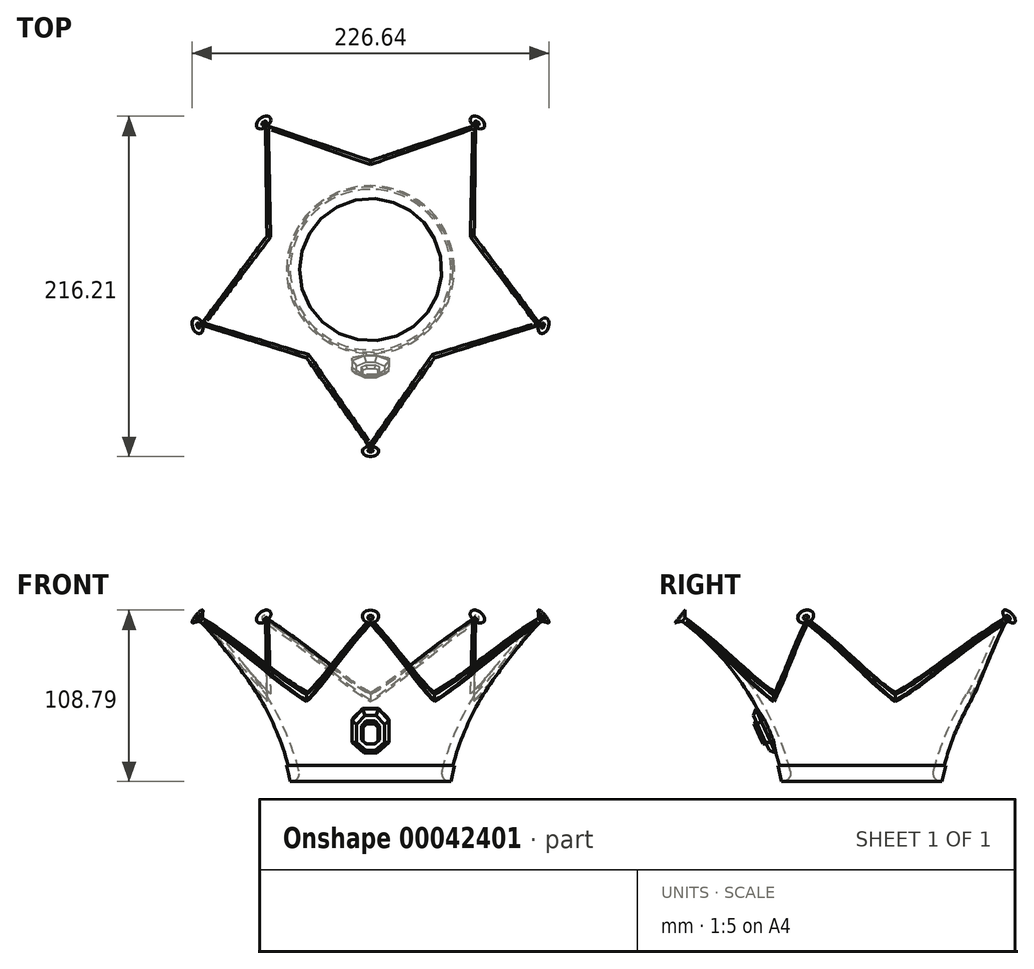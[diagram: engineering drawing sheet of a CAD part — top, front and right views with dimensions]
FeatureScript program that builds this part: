
annotation { "Feature Type Name" : "Feature", "Feature Type Description" : "" }
export const myFeature = defineFeature(function(context is Context, id is Id, definition is map)
    precondition{}
    {
        {
            var Q0;
            Q0=qCreatedBy(makeId("Front.planeOp"),FACE);
            var sketch = newSketch(context, id + "F0", { "sketchPlane" : qUnion([Q0])});
            skLineSegment(sketch, "E0", {"start": v(0, 0) * mm, "end": v(0, 100) * mm, "construction": true});
            skLineSegment(sketch, "E1", {"start": v(0, 0) * mm, "end": v(-50, 0) * mm, "construction": true});
            skArc(sketch, "E2", {"start": v(-50, 0) * mm, "mid": v(-71.94, 55.6) * mm, "end": v(-111.98, 100) * mm});
            skLineSegment(sketch, "E3", {"start": v(-111.98, 100) * mm, "end": v(-214.57, -32.8) * mm, "construction": true});
            skLineSegment(sketch, "E4", {"start": v(-111.98, 100) * mm, "end": v(-110.15, 102.37) * mm});
            skArc(sketch, "E5", {"start": v(-43.88, 0) * mm, "mid": v(-67.74, 57.2) * mm, "end": v(-110.15, 102.37) * mm});
            skLineSegment(sketch, "E6", {"start": v(-50, 0) * mm, "end": v(-43.88, 0) * mm});
            skLineSegment(sketch, "E7", {"start": v(-50, 0) * mm, "end": v(-51, 0) * mm});
            skLineSegment(sketch, "E8", {"start": v(-52.31, 10) * mm, "end": v(-53.31, 10) * mm});
            skLineSegment(sketch, "E9", {"start": v(-53.31, 10) * mm, "end": v(-51, 0) * mm});
            skLineSegment(sketch, "E10", {"start": v(-53.31, 10) * mm, "end": v(-53.31, 0) * mm, "construction": true});
            skSolve(sketch);
        }
        {
            var Q0;
            Q0 = qSketchRegion(id + "F0", true);
            var Q1;
            Q1=sQuery(id+"F0.wireOp",EDGE,"E0");
            revolve(context, id + "F1", {"entities" : qUnion([Q0]), "axis" : qUnion([Q1]), "revolveType" : RevolveType.FULL});
        }
        {
            var Q0;
            Q0=qCreatedBy(makeId("Top.planeOp"),FACE);
            var sketch = newSketch(context, id + "F2", { "sketchPlane" : qUnion([Q0])});
            skLineSegment(sketch, "E11", {"start": v(0, 0) * mm, "end": v(0, -111.98) * mm, "construction": true});
            skCircle(sketch, "E12.0", {"center": v(0, 0) * mm, "radius": 111.98 * mm, "construction": true});
            skLineSegment(sketch, "E13", {"start": v(-1, -111.98) * mm, "end": v(1, -111.98) * mm});
            skLineSegment(sketch, "E14", {"start": v(-1, -111.98) * mm, "end": v(-40.68, -56) * mm});
            skPoint(sketch, "E15", {"position": v(0, -56) * mm});
            skLineSegment(sketch, "E16.MirrorCS", {"start": v(1, -111.98) * mm, "end": v(40.68, -56) * mm});
            skLineSegment(sketch, "E17.1.0", {"start": v(106.2, -35.56) * mm, "end": v(106.8, -33.65) * mm});
            skLineSegment(sketch, "E17.1.1", {"start": v(106.2, -35.56) * mm, "end": v(40.68, -56) * mm});
            skLineSegment(sketch, "E17.1.2", {"start": v(106.8, -33.65) * mm, "end": v(65.82, 21.39) * mm});
            skLineSegment(sketch, "E17.2.0", {"start": v(66.63, 90) * mm, "end": v(65.01, 91.18) * mm});
            skLineSegment(sketch, "E17.2.1", {"start": v(66.63, 90) * mm, "end": v(65.82, 21.39) * mm});
            skLineSegment(sketch, "E17.2.2", {"start": v(65.01, 91.18) * mm, "end": v(0, 69.2) * mm});
            skLineSegment(sketch, "E17.3.0", {"start": v(-65.01, 91.18) * mm, "end": v(-66.63, 90) * mm});
            skLineSegment(sketch, "E17.3.1", {"start": v(-65.01, 91.18) * mm, "end": v(0, 69.2) * mm});
            skLineSegment(sketch, "E17.3.2", {"start": v(-66.63, 90) * mm, "end": v(-65.82, 21.39) * mm});
            skLineSegment(sketch, "E17.4.0", {"start": v(-106.8, -33.65) * mm, "end": v(-106.2, -35.56) * mm});
            skLineSegment(sketch, "E17.4.1", {"start": v(-106.8, -33.65) * mm, "end": v(-65.82, 21.39) * mm});
            skLineSegment(sketch, "E17.4.2", {"start": v(-106.2, -35.56) * mm, "end": v(-40.68, -56) * mm});
            skCircle(sketch, "E18", {"center": v(0, 0) * mm, "radius": 111.99 * mm});
            skCircle(sketch, "E19.0", {"center": v(0, 0) * mm, "radius": 51 * mm, "construction": true});
            skPoint(sketch, "E20", {"position": v(0, -51) * mm});
            skLineSegment(sketch, "E21", {"start": v(0, -56) * mm, "end": v(0, -67) * mm, "construction": true});
            skSolve(sketch);
        }
        {
            var Q0;
            {var subQ2=sQuery(id+"F2.wireOp",EDGE,"E14");Q0=makeQuery(id+"F2.imprint","IMPRINT",FACE,{"disambiguationData":[TD([[makeQuery(id+"F2.imprint","IMPRINT",EDGE,{"derivedFrom":subQ2}),1.0]])]});}
            var Q1;
            {var subQ2=sQuery(id+"F2.wireOp",EDGE,"E16.MirrorCS");Q1=makeQuery(id+"F2.imprint","IMPRINT",FACE,{"disambiguationData":[TD([[makeQuery(id+"F2.imprint","IMPRINT",EDGE,{"derivedFrom":subQ2}),-1.0]])]});}
            var Q2;
            {var subQ2=sQuery(id+"F2.wireOp",EDGE,"E17.1.2");Q2=makeQuery(id+"F2.imprint","IMPRINT",FACE,{"disambiguationData":[TD([[makeQuery(id+"F2.imprint","IMPRINT",EDGE,{"derivedFrom":subQ2}),-1.0]])]});}
            var Q3;
            {var subQ2=sQuery(id+"F2.wireOp",EDGE,"E17.3.2");Q3=makeQuery(id+"F2.imprint","IMPRINT",FACE,{"disambiguationData":[TD([[makeQuery(id+"F2.imprint","IMPRINT",EDGE,{"derivedFrom":subQ2}),-1.0]])]});}
            var Q4;
            {var subQ2=sQuery(id+"F2.wireOp",EDGE,"E17.2.2");Q4=makeQuery(id+"F2.imprint","IMPRINT",FACE,{"disambiguationData":[TD([[makeQuery(id+"F2.imprint","IMPRINT",EDGE,{"derivedFrom":subQ2}),-1.0]])]});}
            extrude(context, id + "F3", {"entities" : qUnion([Q0, Q1, Q2, Q3, Q4]), "operationType" : NewBodyOperationType.REMOVE, "endBound" : BoundingType.THROUGH_ALL, "depth" : 25 * mm});
        }
        {
            var Q0;
            Q0=qCreatedBy(makeId("Right.planeOp"),FACE);
            var sketch = newSketch(context, id + "F4", { "sketchPlane" : qUnion([Q0])});
            skPoint(sketch, "E22.0", {"position": v(-110.12, 102.37) * mm});
            skPoint(sketch, "E23.0", {"position": v(-111.98, 100) * mm});
            skLineSegment(sketch, "E24", {"start": v(-110.12, 102.37) * mm, "end": v(-111.98, 100) * mm, "construction": true});
            skLineSegment(sketch, "E25", {"start": v(-111.05, 101.19) * mm, "end": v(-122.87, 110.42) * mm});
            skLineSegment(sketch, "E26", {"start": v(-111.05, 101.19) * mm, "end": v(-110.12, 102.37) * mm});
            skLineSegment(sketch, "E27", {"start": v(-110.12, 102.37) * mm, "end": v(-112.2, 104) * mm});
            skArc(sketch, "E28", {"start": v(-112.3, 108.8) * mm, "mid": v(-112.44, 106.39) * mm, "end": v(-112.2, 104) * mm});
            skLineSegment(sketch, "E29", {"start": v(-112.3, 108.8) * mm, "end": v(-112.3, 108.8) * mm});
            skArc(sketch, "E30", {"start": v(-113.84, 105.52) * mm, "mid": v(-112.9, 107.07) * mm, "end": v(-112.3, 108.8) * mm});
            skArc(sketch, "E31", {"start": v(-113.84, 105.52) * mm, "mid": v(-116.12, 112.09) * mm, "end": v(-122.87, 110.42) * mm});
            skSolve(sketch);
        }
        {
            var Q0;
            Q0 = qSketchRegion(id + "F4", true);
            var Q1;
            Q1=sQuery(id+"F4.wireOp",EDGE,"E25");
            revolve(context, id + "F5", {"entities" : qUnion([Q0]), "axis" : qUnion([Q1]), "revolveType" : RevolveType.FULL});
        }
        {
            var Q0;
            Q0=makeQuery(id+"F5.opRevolve","SWEPT_BODY",BODY,{"disambiguationData":[OSD([sQuery(id+"F4.wireOp",EDGE,"E25"),sQuery(id+"F4.wireOp",EDGE,"E26"),sQuery(id+"F4.wireOp",EDGE,"E27"),sQuery(id+"F4.wireOp",EDGE,"E28"),sQuery(id+"F4.wireOp",EDGE,"E30"),sQuery(id+"F4.wireOp",EDGE,"E31")])]});
            var Q1;
            Q1=sQuery(id+"F0.wireOp",EDGE,"E0");
            circularPattern(context, id + "F6", {"operationType" : NewBodyOperationType.ADD, "entities" : qUnion([Q0]), "axis" : qUnion([Q1]), "angle" : 72 * degree, "instanceCount" : 5});
        }
        {
            var Q0;
            Q0=makeQuery(id+"F3.boolean.opBoolean","INTERSECT",VERTEX,{"derivedFrom":[makeQuery(id+"F1.opRevolve","SWEPT_FACE",FACE,{"disambiguationData":[OSD([sQuery(id+"F0.wireOp",EDGE,"E2")])]}),makeQuery(id+"F1.opRevolve","SWEPT_FACE",FACE,{"disambiguationData":[OSD([sQuery(id+"F0.wireOp",EDGE,"E4")])]}),makeQuery(id+"F3.opExtrude","SWEPT_FACE",FACE,{"disambiguationData":[OSD([sQuery(id+"F2.wireOp",EDGE,"E14")])]})]});
            var Q1;
            Q1=makeQuery(id+"F3.boolean.opBoolean","INTERSECT",VERTEX,{"derivedFrom":[makeQuery(id+"F1.opRevolve","SWEPT_FACE",FACE,{"disambiguationData":[OSD([sQuery(id+"F0.wireOp",EDGE,"E2")])]}),makeQuery(id+"F1.opRevolve","SWEPT_FACE",FACE,{"disambiguationData":[OSD([sQuery(id+"F0.wireOp",EDGE,"E4")])]}),makeQuery(id+"F3.opExtrude","SWEPT_FACE",FACE,{"disambiguationData":[OSD([sQuery(id+"F2.wireOp",EDGE,"E16.MirrorCS")])]})]});
            var Q2;
            Q2=sQuery(id+"F2.wireOp",VERTEX,"E21.end");
            cPlane(context, id + "F7", {"entities" : qUnion([Q0, Q1, Q2]), "cplaneType" : CPlaneType.THREE_POINT, "offset" : 150 * mm, "width" : 150 * mm, "height" : 150 * mm});
        }
        {
            var Q0;
            Q0=qCreatedBy(id+"F7.planeOp",FACE);
            cPlane(context, id + "F8", {"entities" : qUnion([Q0]), "cplaneType" : CPlaneType.OFFSET, "offset" : 20 * mm, "oppositeDirection" : true, "width" : 150 * mm, "height" : 150 * mm});
        }
        {
            var Q0;
            Q0=qCreatedBy(id+"F8.planeOp",FACE);
            var sketch = newSketch(context, id + "F9", { "sketchPlane" : qUnion([Q0])});
            skLineSegment(sketch, "E32.0", {"start": v(0, 0) * mm, "end": v(0, 91.2) * mm, "construction": true});
            skLineSegment(sketch, "E33.0", {"start": v(-1, 45.94) * mm, "end": v(1, 45.94) * mm, "construction": true});
            skPoint(sketch, "E34.0", {"position": v(-40.68, 69.52) * mm});
            skPoint(sketch, "E35.0", {"position": v(40.68, 69.52) * mm});
            skLineSegment(sketch, "E36", {"start": v(-40.68, 69.52) * mm, "end": v(40.68, 69.52) * mm, "construction": true});
            skLineSegment(sketch, "E37", {"start": v(-5, 69.52) * mm, "end": v(5, 69.52) * mm});
            skPoint(sketch, "E38", {"position": v(0, 69.52) * mm});
            skLineSegment(sketch, "E39", {"start": v(-5, 69.52) * mm, "end": v(-11.83, 61.33) * mm});
            skLineSegment(sketch, "E40", {"start": v(-11.83, 61.33) * mm, "end": v(-11.83, 46.33) * mm});
            skLineSegment(sketch, "E41", {"start": v(-11.83, 46.33) * mm, "end": v(-4.17, 38.9) * mm});
            skLineSegment(sketch, "E42", {"start": v(-4.17, 38.9) * mm, "end": v(0, 38.9) * mm});
            skLineSegment(sketch, "E43.MirrorCS", {"start": v(5, 69.52) * mm, "end": v(11.83, 61.33) * mm});
            skLineSegment(sketch, "E44.MirrorCS", {"start": v(11.83, 61.33) * mm, "end": v(11.83, 46.33) * mm});
            skLineSegment(sketch, "E45.MirrorCS", {"start": v(11.83, 46.33) * mm, "end": v(4.17, 38.9) * mm});
            skLineSegment(sketch, "E46.MirrorCS", {"start": v(4.17, 38.9) * mm, "end": v(0, 38.9) * mm});
            skSolve(sketch);
        }
        {
            var Q0;
            Q0 = qSketchRegion(id + "F9", true);
            extrude(context, id + "F10", {"entities" : qUnion([Q0]), "operationType" : NewBodyOperationType.ADD, "depth" : 4.5 * mm, "hasSecondDirection" : true, "secondDirectionOppositeDirection" : true, "secondDirectionDepth" : 1 * mm});
        }
        {
            var Q0;
            Q0=makeQuery(id+"F10.opExtrude","CAP_EDGE",EDGE,{"disambiguationData":[OSD([sQuery(id+"F9.wireOp",EDGE,"E37")])],"isStart":false});
            var Q1;
            Q1=makeQuery(id+"F10.opExtrude","CAP_EDGE",EDGE,{"disambiguationData":[OSD([sQuery(id+"F9.wireOp",EDGE,"E39")])],"isStart":false});
            var Q2;
            Q2=makeQuery(id+"F10.opExtrude","CAP_EDGE",EDGE,{"disambiguationData":[OSD([sQuery(id+"F9.wireOp",EDGE,"E43.MirrorCS")])],"isStart":false});
            var Q3;
            Q3=makeQuery(id+"F10.opExtrude","CAP_EDGE",EDGE,{"disambiguationData":[OSD([sQuery(id+"F9.wireOp",EDGE,"E44.MirrorCS")])],"isStart":false});
            var Q4;
            Q4=makeQuery(id+"F10.opExtrude","CAP_EDGE",EDGE,{"disambiguationData":[OSD([sQuery(id+"F9.wireOp",EDGE,"E45.MirrorCS")])],"isStart":false});
            var Q5;
            Q5=makeQuery(id+"F10.opExtrude","CAP_EDGE",EDGE,{"disambiguationData":[OSD([sQuery(id+"F9.wireOp",EDGE,"E41")])],"isStart":false});
            var Q6;
            Q6=makeQuery(id+"F10.opExtrude","CAP_EDGE",EDGE,{"disambiguationData":[OSD([sQuery(id+"F9.wireOp",EDGE,"E42"),sQuery(id+"F9.wireOp",EDGE,"E46.MirrorCS")])],"isStart":false});
            var Q7;
            Q7=makeQuery(id+"F10.opExtrude","CAP_EDGE",EDGE,{"disambiguationData":[OSD([sQuery(id+"F9.wireOp",EDGE,"E40")])],"isStart":false});
            chamfer(context, id + "F11", {"entities" : qUnion([Q0, Q1, Q2, Q3, Q4, Q5, Q6, Q7]), "width" : 3 * mm, "tangentPropagation" : true});
        }
        {
            var Q0;
            Q0=makeQuery(id+"F10.opExtrude","CAP_FACE",FACE,{"disambiguationData":[OSD([sQuery(id+"F9.wireOp",EDGE,"E37"),sQuery(id+"F9.wireOp",EDGE,"E39"),sQuery(id+"F9.wireOp",EDGE,"E40"),sQuery(id+"F9.wireOp",EDGE,"E41"),sQuery(id+"F9.wireOp",EDGE,"E42"),sQuery(id+"F9.wireOp",EDGE,"E43.MirrorCS"),sQuery(id+"F9.wireOp",EDGE,"E44.MirrorCS"),sQuery(id+"F9.wireOp",EDGE,"E45.MirrorCS"),sQuery(id+"F9.wireOp",EDGE,"E46.MirrorCS")])],"isStart":false});
            var sketch = newSketch(context, id + "F12", { "sketchPlane" : qUnion([Q0])});
            skLineSegment(sketch, "E47", {"start": v(-3, 62.47) * mm, "end": v(0, 62.47) * mm});
            skLineSegment(sketch, "E48", {"start": v(-3, 62.47) * mm, "end": v(-5.72, 59.21) * mm});
            skLineSegment(sketch, "E49", {"start": v(-5.72, 49.21) * mm, "end": v(-3, 46.58) * mm});
            skLineSegment(sketch, "E50", {"start": v(-3, 46.58) * mm, "end": v(0, 46.58) * mm});
            skLineSegment(sketch, "E51", {"start": v(0, 66.52) * mm, "end": v(0, 41.9) * mm, "construction": true});
            skLineSegment(sketch, "E52", {"start": v(-5.72, 54.21) * mm, "end": v(0, 54.21) * mm, "construction": true});
            skLineSegment(sketch, "E53", {"start": v(-5.72, 59.21) * mm, "end": v(-5.72, 49.21) * mm});
            skLineSegment(sketch, "E54.MirrorCS", {"start": v(3, 62.47) * mm, "end": v(0, 62.47) * mm});
            skLineSegment(sketch, "E55.MirrorCS", {"start": v(3, 62.47) * mm, "end": v(5.72, 59.21) * mm});
            skLineSegment(sketch, "E56.MirrorCS", {"start": v(5.72, 59.21) * mm, "end": v(5.72, 49.21) * mm});
            skLineSegment(sketch, "E57.MirrorCS", {"start": v(5.72, 49.21) * mm, "end": v(3, 46.58) * mm});
            skLineSegment(sketch, "E58.MirrorCS", {"start": v(3, 46.58) * mm, "end": v(0, 46.58) * mm});
            skSolve(sketch);
        }
        {
            var Q0;
            Q0=makeQuery(id+"F12.imprint","IMPRINT",FACE,{"disambiguationData":[TD([[makeQuery(id+"F12.imprint","IMPRINT",EDGE,{"derivedFrom":sQuery(id+"F12.wireOp",EDGE,"E47")}),1.0]])]});
            cPlane(context, id + "F13", {"entities" : qUnion([Q0]), "cplaneType" : CPlaneType.OFFSET, "offset" : 2 * mm, "width" : 150 * mm, "height" : 150 * mm});
        }
        {
            var Q0;
            Q0=qCreatedBy(id+"F13.planeOp",FACE);
            var sketch = newSketch(context, id + "F14", { "sketchPlane" : qUnion([Q0])});
            skLineSegment(sketch, "E59.0", {"start": v(-3, 62.47) * mm, "end": v(-5.72, 59.21) * mm, "construction": true});
            skLineSegment(sketch, "E60.0", {"start": v(-3, 62.47) * mm, "end": v(0, 62.47) * mm, "construction": true});
            skLineSegment(sketch, "E61.0", {"start": v(3, 62.47) * mm, "end": v(0, 62.47) * mm, "construction": true});
            skLineSegment(sketch, "E62.0", {"start": v(3, 62.47) * mm, "end": v(5.72, 59.21) * mm, "construction": true});
            skLineSegment(sketch, "E63.0", {"start": v(5.72, 59.21) * mm, "end": v(5.72, 49.21) * mm, "construction": true});
            skLineSegment(sketch, "E64.0", {"start": v(5.72, 49.21) * mm, "end": v(3, 46.58) * mm, "construction": true});
            skLineSegment(sketch, "E65.0", {"start": v(3, 46.58) * mm, "end": v(0, 46.58) * mm, "construction": true});
            skLineSegment(sketch, "E66.0", {"start": v(-3, 46.58) * mm, "end": v(0, 46.58) * mm, "construction": true});
            skLineSegment(sketch, "E67.0", {"start": v(-5.72, 49.21) * mm, "end": v(-3, 46.58) * mm, "construction": true});
            skLineSegment(sketch, "E68.0", {"start": v(-5.72, 59.21) * mm, "end": v(-5.72, 49.21) * mm, "construction": true});
            skLineSegment(sketch, "E69.0", {"start": v(-2.53, 61.47) * mm, "end": v(0, 61.47) * mm});
            skLineSegment(sketch, "E69.1", {"start": v(2.53, 61.47) * mm, "end": v(0, 61.47) * mm});
            skLineSegment(sketch, "E69.2", {"start": v(-2.53, 61.47) * mm, "end": v(-4.72, 58.85) * mm});
            skLineSegment(sketch, "E69.3", {"start": v(2.53, 61.47) * mm, "end": v(4.72, 58.85) * mm});
            skLineSegment(sketch, "E69.4", {"start": v(4.72, 58.85) * mm, "end": v(4.72, 49.63) * mm});
            skLineSegment(sketch, "E69.5", {"start": v(4.72, 49.63) * mm, "end": v(2.6, 47.58) * mm});
            skLineSegment(sketch, "E69.6", {"start": v(-4.72, 58.85) * mm, "end": v(-4.72, 49.63) * mm});
            skLineSegment(sketch, "E69.7", {"start": v(-4.72, 49.63) * mm, "end": v(-2.6, 47.58) * mm});
            skLineSegment(sketch, "E69.8", {"start": v(-2.6, 47.58) * mm, "end": v(0, 47.58) * mm});
            skLineSegment(sketch, "E69.9", {"start": v(2.6, 47.58) * mm, "end": v(0, 47.58) * mm});
            skSolve(sketch);
        }
        {
            var Q1;
            Q1=makeQuery(id+"F12.imprint","IMPRINT",FACE,{"disambiguationData":[TD([[makeQuery(id+"F12.imprint","IMPRINT",EDGE,{"derivedFrom":sQuery(id+"F12.wireOp",EDGE,"E47")}),-1.0]])]});
            var Q2;
            Q2=makeQuery(id+"F14.imprint","IMPRINT",FACE,{"disambiguationData":[TD([[makeQuery(id+"F14.imprint","IMPRINT",EDGE,{"derivedFrom":sQuery(id+"F14.wireOp",EDGE,"E69.0")}),-1.0]])]});
            loft(context, id + "F15", {"operationType" : NewBodyOperationType.ADD, "sheetProfilesArray" : [{ "sheetProfileEntities" : qUnion([Q1]) }, { "sheetProfileEntities" : qUnion([Q2]) }]});
        }
        {
            var Q0;
            Q0=makeQuery(id+"F1.opRevolve","SWEPT_EDGE",EDGE,{"disambiguationData":[OSD([sQuery(id+"F0.wireOp",EDGE,"E5"),sQuery(id+"F0.wireOp",EDGE,"E6")])]});
            fillet(context, id + "F16", {"entities" : qUnion([Q0]), "radius" : 5 * mm, "tangentPropagation" : true, "allowEdgeOverflow" : false});
        }
        {
            var Q0;
            Q0=makeQuery(id+"F3.boolean.opBoolean","INTERSECT",EDGE,{"derivedFrom":[makeQuery(id+"F1.opRevolve","SWEPT_FACE",FACE,{"disambiguationData":[OSD([sQuery(id+"F0.wireOp",EDGE,"E2")])]}),makeQuery(id+"F3.opExtrude","SWEPT_FACE",FACE,{"disambiguationData":[OSD([sQuery(id+"F2.wireOp",EDGE,"E16.MirrorCS")])]})]});
            var Q1;
            Q1=makeQuery(id+"F3.boolean.opBoolean","INTERSECT",EDGE,{"derivedFrom":[makeQuery(id+"F1.opRevolve","SWEPT_FACE",FACE,{"disambiguationData":[OSD([sQuery(id+"F0.wireOp",EDGE,"E2")])]}),makeQuery(id+"F3.opExtrude","SWEPT_FACE",FACE,{"disambiguationData":[OSD([sQuery(id+"F2.wireOp",EDGE,"E14")])]})]});
            var Q2;
            Q2=makeQuery(id+"F3.boolean.opBoolean","INTERSECT",EDGE,{"derivedFrom":[makeQuery(id+"F1.opRevolve","SWEPT_FACE",FACE,{"disambiguationData":[OSD([sQuery(id+"F0.wireOp",EDGE,"E5")])]}),makeQuery(id+"F3.opExtrude","SWEPT_FACE",FACE,{"disambiguationData":[OSD([sQuery(id+"F2.wireOp",EDGE,"E14")])]})]});
            var Q3;
            Q3=makeQuery(id+"F3.boolean.opBoolean","INTERSECT",EDGE,{"derivedFrom":[makeQuery(id+"F1.opRevolve","SWEPT_FACE",FACE,{"disambiguationData":[OSD([sQuery(id+"F0.wireOp",EDGE,"E5")])]}),makeQuery(id+"F3.opExtrude","SWEPT_FACE",FACE,{"disambiguationData":[OSD([sQuery(id+"F2.wireOp",EDGE,"E16.MirrorCS")])]})]});
            var Q4;
            Q4=makeQuery(id+"F3.boolean.opBoolean","INTERSECT",EDGE,{"derivedFrom":[makeQuery(id+"F1.opRevolve","SWEPT_FACE",FACE,{"disambiguationData":[OSD([sQuery(id+"F0.wireOp",EDGE,"E2")])]}),makeQuery(id+"F3.opExtrude","SWEPT_FACE",FACE,{"disambiguationData":[OSD([sQuery(id+"F2.wireOp",EDGE,"E17.4.2")])]})]});
            var Q5;
            Q5=makeQuery(id+"F3.boolean.opBoolean","INTERSECT",EDGE,{"derivedFrom":[makeQuery(id+"F1.opRevolve","SWEPT_FACE",FACE,{"disambiguationData":[OSD([sQuery(id+"F0.wireOp",EDGE,"E5")])]}),makeQuery(id+"F3.opExtrude","SWEPT_FACE",FACE,{"disambiguationData":[OSD([sQuery(id+"F2.wireOp",EDGE,"E17.4.2")])]})]});
            var Q6;
            Q6=makeQuery(id+"F3.boolean.opBoolean","INTERSECT",EDGE,{"derivedFrom":[makeQuery(id+"F1.opRevolve","SWEPT_FACE",FACE,{"disambiguationData":[OSD([sQuery(id+"F0.wireOp",EDGE,"E2")])]}),makeQuery(id+"F3.opExtrude","SWEPT_FACE",FACE,{"disambiguationData":[OSD([sQuery(id+"F2.wireOp",EDGE,"E17.4.1")])]})]});
            var Q7;
            Q7=makeQuery(id+"F3.boolean.opBoolean","INTERSECT",EDGE,{"derivedFrom":[makeQuery(id+"F1.opRevolve","SWEPT_FACE",FACE,{"disambiguationData":[OSD([sQuery(id+"F0.wireOp",EDGE,"E5")])]}),makeQuery(id+"F3.opExtrude","SWEPT_FACE",FACE,{"disambiguationData":[OSD([sQuery(id+"F2.wireOp",EDGE,"E17.4.1")])]})]});
            var Q8;
            Q8=makeQuery(id+"F3.boolean.opBoolean","INTERSECT",EDGE,{"derivedFrom":[makeQuery(id+"F1.opRevolve","SWEPT_FACE",FACE,{"disambiguationData":[OSD([sQuery(id+"F0.wireOp",EDGE,"E2")])]}),makeQuery(id+"F3.opExtrude","SWEPT_FACE",FACE,{"disambiguationData":[OSD([sQuery(id+"F2.wireOp",EDGE,"E17.3.2")])]})]});
            var Q9;
            Q9=makeQuery(id+"F3.boolean.opBoolean","INTERSECT",EDGE,{"derivedFrom":[makeQuery(id+"F1.opRevolve","SWEPT_FACE",FACE,{"disambiguationData":[OSD([sQuery(id+"F0.wireOp",EDGE,"E5")])]}),makeQuery(id+"F3.opExtrude","SWEPT_FACE",FACE,{"disambiguationData":[OSD([sQuery(id+"F2.wireOp",EDGE,"E17.3.2")])]})]});
            var Q10;
            Q10=makeQuery(id+"F3.boolean.opBoolean","INTERSECT",EDGE,{"derivedFrom":[makeQuery(id+"F1.opRevolve","SWEPT_FACE",FACE,{"disambiguationData":[OSD([sQuery(id+"F0.wireOp",EDGE,"E5")])]}),makeQuery(id+"F3.opExtrude","SWEPT_FACE",FACE,{"disambiguationData":[OSD([sQuery(id+"F2.wireOp",EDGE,"E17.1.1")])]})]});
            var Q11;
            Q11=makeQuery(id+"F3.boolean.opBoolean","INTERSECT",EDGE,{"derivedFrom":[makeQuery(id+"F1.opRevolve","SWEPT_FACE",FACE,{"disambiguationData":[OSD([sQuery(id+"F0.wireOp",EDGE,"E2")])]}),makeQuery(id+"F3.opExtrude","SWEPT_FACE",FACE,{"disambiguationData":[OSD([sQuery(id+"F2.wireOp",EDGE,"E17.1.1")])]})]});
            var Q12;
            Q12=makeQuery(id+"F3.boolean.opBoolean","INTERSECT",EDGE,{"derivedFrom":[makeQuery(id+"F1.opRevolve","SWEPT_FACE",FACE,{"disambiguationData":[OSD([sQuery(id+"F0.wireOp",EDGE,"E5")])]}),makeQuery(id+"F3.opExtrude","SWEPT_FACE",FACE,{"disambiguationData":[OSD([sQuery(id+"F2.wireOp",EDGE,"E17.1.2")])]})]});
            var Q13;
            Q13=makeQuery(id+"F3.boolean.opBoolean","INTERSECT",EDGE,{"derivedFrom":[makeQuery(id+"F1.opRevolve","SWEPT_FACE",FACE,{"disambiguationData":[OSD([sQuery(id+"F0.wireOp",EDGE,"E2")])]}),makeQuery(id+"F3.opExtrude","SWEPT_FACE",FACE,{"disambiguationData":[OSD([sQuery(id+"F2.wireOp",EDGE,"E17.1.2")])]})]});
            var Q14;
            Q14=makeQuery(id+"F3.boolean.opBoolean","INTERSECT",EDGE,{"derivedFrom":[makeQuery(id+"F1.opRevolve","SWEPT_FACE",FACE,{"disambiguationData":[OSD([sQuery(id+"F0.wireOp",EDGE,"E2")])]}),makeQuery(id+"F3.opExtrude","SWEPT_FACE",FACE,{"disambiguationData":[OSD([sQuery(id+"F2.wireOp",EDGE,"E17.2.1")])]})]});
            var Q15;
            Q15=makeQuery(id+"F3.boolean.opBoolean","INTERSECT",EDGE,{"derivedFrom":[makeQuery(id+"F1.opRevolve","SWEPT_FACE",FACE,{"disambiguationData":[OSD([sQuery(id+"F0.wireOp",EDGE,"E5")])]}),makeQuery(id+"F3.opExtrude","SWEPT_FACE",FACE,{"disambiguationData":[OSD([sQuery(id+"F2.wireOp",EDGE,"E17.2.1")])]})]});
            var Q16;
            Q16=makeQuery(id+"F3.boolean.opBoolean","INTERSECT",EDGE,{"derivedFrom":[makeQuery(id+"F1.opRevolve","SWEPT_FACE",FACE,{"disambiguationData":[OSD([sQuery(id+"F0.wireOp",EDGE,"E2")])]}),makeQuery(id+"F3.opExtrude","SWEPT_FACE",FACE,{"disambiguationData":[OSD([sQuery(id+"F2.wireOp",EDGE,"E17.2.2")])]})]});
            var Q17;
            Q17=makeQuery(id+"F3.boolean.opBoolean","INTERSECT",EDGE,{"derivedFrom":[makeQuery(id+"F1.opRevolve","SWEPT_FACE",FACE,{"disambiguationData":[OSD([sQuery(id+"F0.wireOp",EDGE,"E5")])]}),makeQuery(id+"F3.opExtrude","SWEPT_FACE",FACE,{"disambiguationData":[OSD([sQuery(id+"F2.wireOp",EDGE,"E17.2.2")])]})]});
            var Q18;
            Q18=makeQuery(id+"F3.boolean.opBoolean","INTERSECT",EDGE,{"derivedFrom":[makeQuery(id+"F1.opRevolve","SWEPT_FACE",FACE,{"disambiguationData":[OSD([sQuery(id+"F0.wireOp",EDGE,"E2")])]}),makeQuery(id+"F3.opExtrude","SWEPT_FACE",FACE,{"disambiguationData":[OSD([sQuery(id+"F2.wireOp",EDGE,"E17.3.1")])]})]});
            var Q19;
            Q19=makeQuery(id+"F3.boolean.opBoolean","INTERSECT",EDGE,{"derivedFrom":[makeQuery(id+"F1.opRevolve","SWEPT_FACE",FACE,{"disambiguationData":[OSD([sQuery(id+"F0.wireOp",EDGE,"E5")])]}),makeQuery(id+"F3.opExtrude","SWEPT_FACE",FACE,{"disambiguationData":[OSD([sQuery(id+"F2.wireOp",EDGE,"E17.3.1")])]})]});
            fillet(context, id + "F17", {"entities" : qUnion([Q0, Q1, Q2, Q3, Q4, Q5, Q6, Q7, Q8, Q9, Q10, Q11, Q12, Q13, Q14, Q15, Q16, Q17, Q18, Q19]), "radius" : 1.3 * mm, "tangentPropagation" : true, "allowEdgeOverflow" : false});
        }
    });
